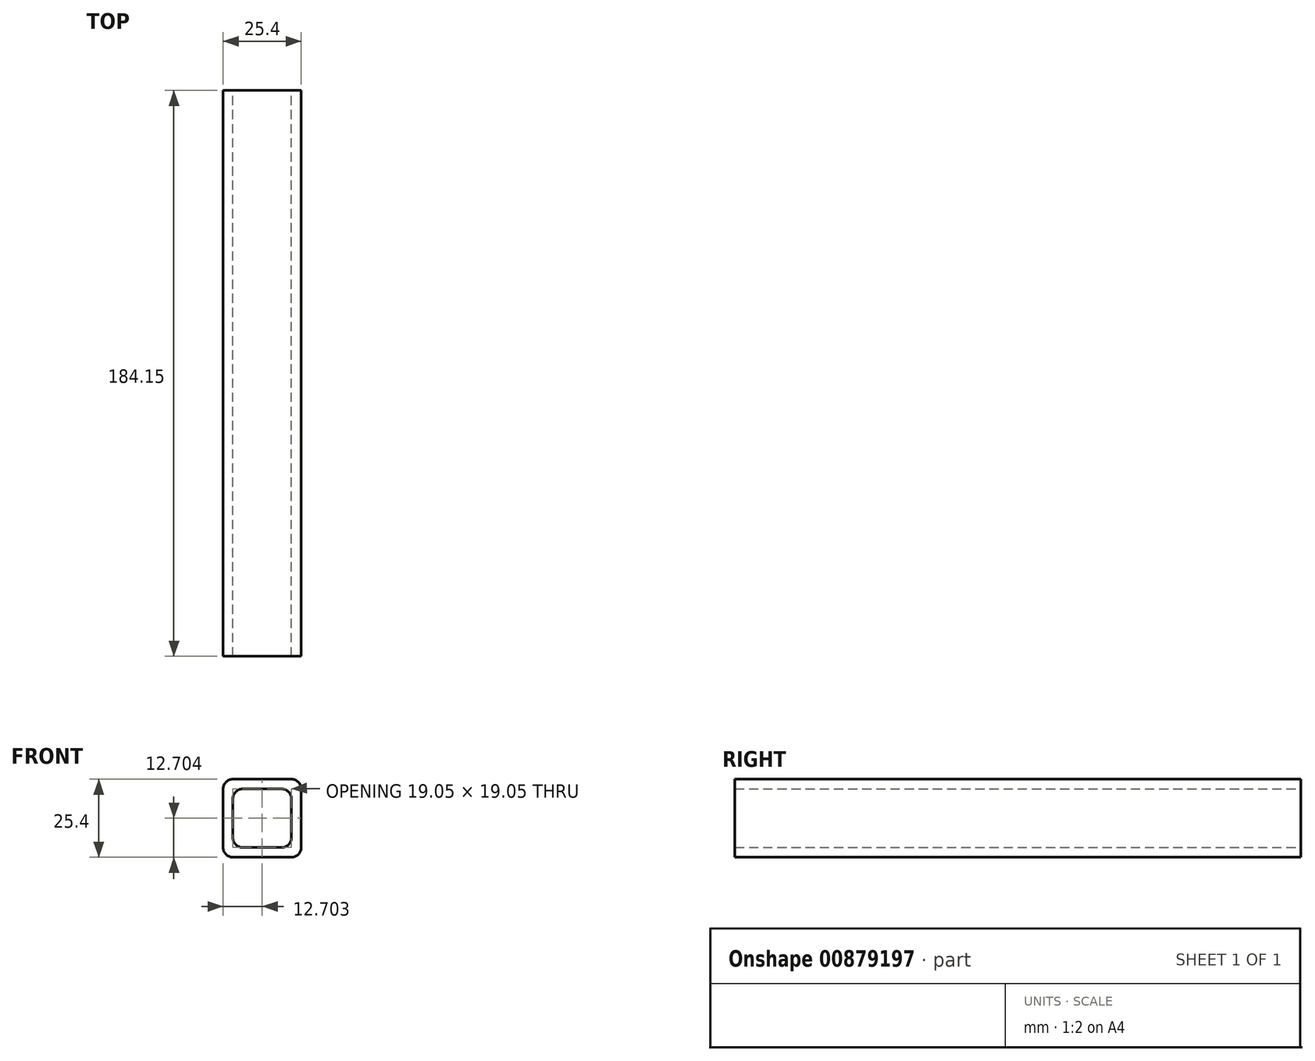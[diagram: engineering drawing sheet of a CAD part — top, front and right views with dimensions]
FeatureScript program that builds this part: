
annotation { "Feature Type Name" : "Feature", "Feature Type Description" : "" }
export const myFeature = defineFeature(function(context is Context, id is Id, definition is map)
    precondition{}
    {
        {
            var Q0;
            Q0=qCreatedBy(makeId("Front.planeOp"),FACE);
            var sketch = newSketch(context, id + "F0", { "sketchPlane" : qUnion([Q0])});
            skLineSegment(sketch, "E0.bottom", {"start": v(8.96, -12.6) * mm, "end": v(-10.1, -12.6) * mm});
            skLineSegment(sketch, "E0.top", {"start": v(8.96, 12.8) * mm, "end": v(-10.1, 12.8) * mm});
            skLineSegment(sketch, "E0.left", {"start": v(12.13, -9.43) * mm, "end": v(12.13, 9.62) * mm});
            skLineSegment(sketch, "E0.right", {"start": v(-13.27, -9.43) * mm, "end": v(-13.27, 9.62) * mm});
            skLineSegment(sketch, "E1.bottom", {"start": v(5.78, -9.43) * mm, "end": v(-6.92, -9.43) * mm});
            skLineSegment(sketch, "E1.top", {"start": v(5.78, 9.62) * mm, "end": v(-6.92, 9.62) * mm});
            skLineSegment(sketch, "E1.left", {"start": v(8.96, -6.26) * mm, "end": v(8.96, 6.44) * mm});
            skLineSegment(sketch, "E1.right", {"start": v(-10.1, -6.26) * mm, "end": v(-10.1, 6.44) * mm});
            skPoint(sketch, "E2.visualSharp", {"position": v(8.96, 9.62) * mm});
            skArc(sketch, "E2.filletArc", {"start": v(8.96, 6.44) * mm, "mid": v(8.03, 8.69) * mm, "end": v(5.78, 9.62) * mm});
            skPoint(sketch, "E3.visualSharp", {"position": v(-10.1, 9.62) * mm});
            skArc(sketch, "E3.filletArc", {"start": v(-6.92, 9.62) * mm, "mid": v(-9.16, 8.69) * mm, "end": v(-10.1, 6.44) * mm});
            skPoint(sketch, "E4.visualSharp", {"position": v(-10.1, -9.43) * mm});
            skArc(sketch, "E4.filletArc", {"start": v(-10.1, -6.26) * mm, "mid": v(-9.16, -8.5) * mm, "end": v(-6.92, -9.43) * mm});
            skPoint(sketch, "E5.visualSharp", {"position": v(8.96, -9.43) * mm});
            skArc(sketch, "E5.filletArc", {"start": v(5.78, -9.43) * mm, "mid": v(8.03, -8.5) * mm, "end": v(8.96, -6.26) * mm});
            skPoint(sketch, "E6.visualSharp", {"position": v(12.13, 12.8) * mm});
            skArc(sketch, "E6.filletArc", {"start": v(12.13, 9.62) * mm, "mid": v(11.2, 11.86) * mm, "end": v(8.96, 12.8) * mm});
            skPoint(sketch, "E7.visualSharp", {"position": v(-13.27, 12.8) * mm});
            skArc(sketch, "E7.filletArc", {"start": v(-10.1, 12.8) * mm, "mid": v(-12.34, 11.86) * mm, "end": v(-13.27, 9.62) * mm});
            skPoint(sketch, "E8.visualSharp", {"position": v(-13.27, -12.6) * mm});
            skArc(sketch, "E8.filletArc", {"start": v(-13.27, -9.43) * mm, "mid": v(-12.34, -11.68) * mm, "end": v(-10.1, -12.6) * mm});
            skPoint(sketch, "E9.visualSharp", {"position": v(12.13, -12.6) * mm});
            skArc(sketch, "E9.filletArc", {"start": v(8.96, -12.6) * mm, "mid": v(11.2, -11.68) * mm, "end": v(12.13, -9.43) * mm});
            skSolve(sketch);
        }
        {
            var Q0;
            Q0=qSketchRegion(id+"F0",true);
            extrude(context, id + "F1", {"entities" : qUnion([Q0]), "depth" : 184.15 * mm, "offsetDistance" : 25.4 * mm});
        }
    });
